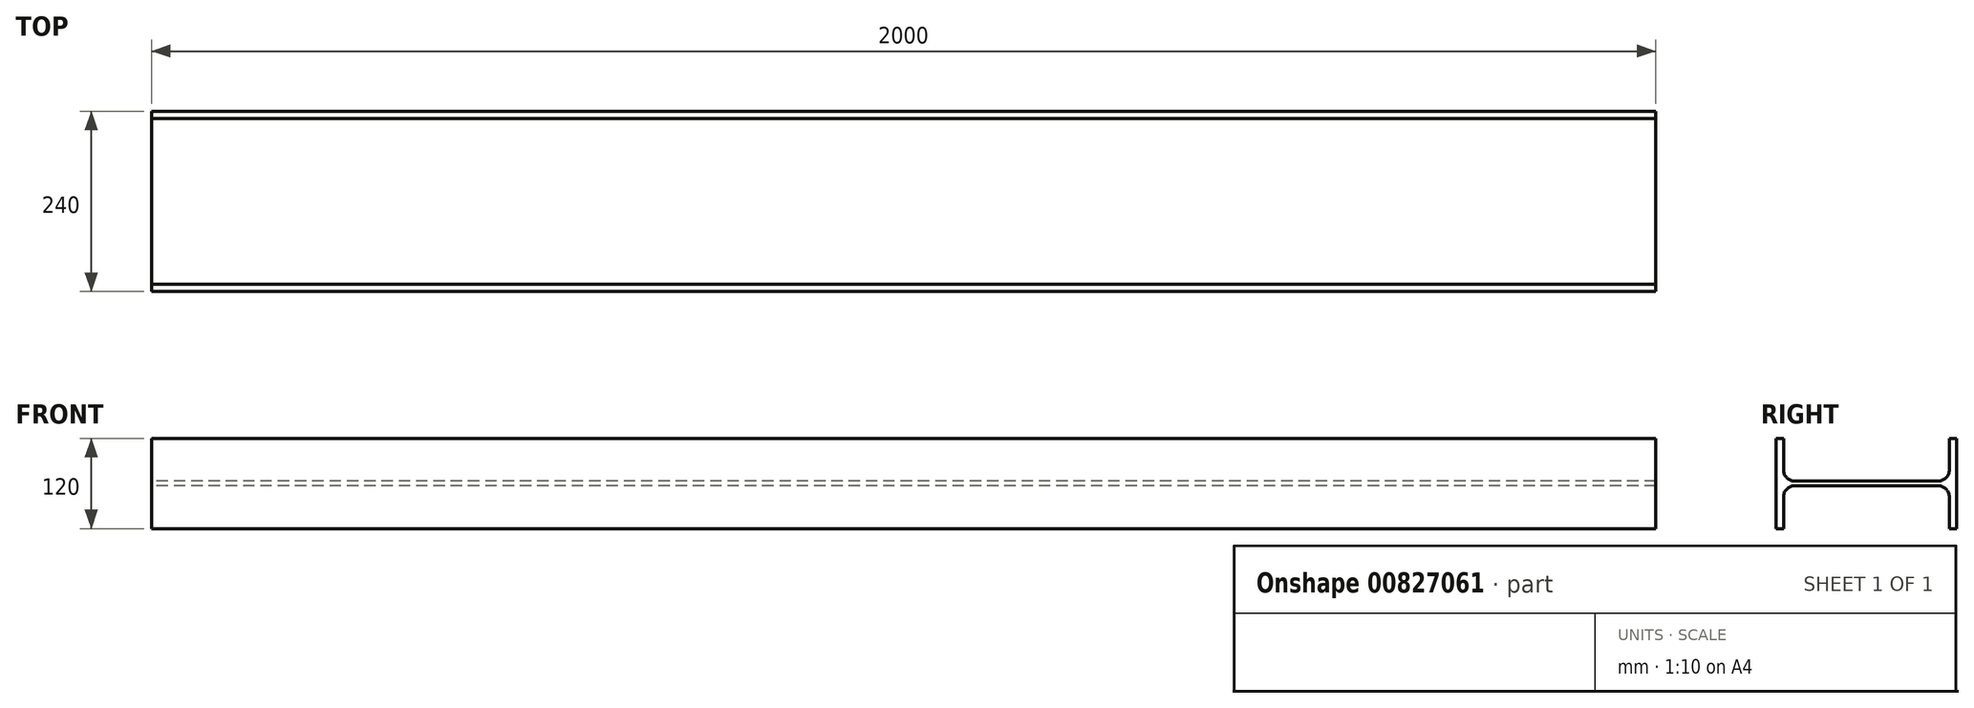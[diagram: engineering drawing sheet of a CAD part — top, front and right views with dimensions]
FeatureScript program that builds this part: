
annotation { "Feature Type Name" : "Feature", "Feature Type Description" : "" }
export const myFeature = defineFeature(function(context is Context, id is Id, definition is map)
    precondition{}
    {
        {
            var Q0;
            Q0=qCreatedBy(makeId("Right.planeOp"),FACE);
            var sketch = newSketch(context, id + "F0", { "sketchPlane" : qUnion([Q0])});
            skLineSegment(sketch, "E0", {"start": v(120, 0) * mm, "end": v(-120, 0) * mm, "construction": true});
            skLineSegment(sketch, "E1", {"start": v(120, 60) * mm, "end": v(120, -60) * mm});
            skLineSegment(sketch, "E2", {"start": v(-120, 60) * mm, "end": v(-120, -60) * mm});
            skLineSegment(sketch, "E3", {"start": v(-120, -60) * mm, "end": v(-110.2, -60) * mm});
            skLineSegment(sketch, "E4", {"start": v(-110.2, -60) * mm, "end": v(-110.2, -18.1) * mm});
            skLineSegment(sketch, "E5", {"start": v(-110.2, 60) * mm, "end": v(-120, 60) * mm});
            skLineSegment(sketch, "E6", {"start": v(120, 60) * mm, "end": v(110.2, 60) * mm});
            skLineSegment(sketch, "E7", {"start": v(110.2, 60) * mm, "end": v(110.2, 18.1) * mm});
            skLineSegment(sketch, "E8", {"start": v(110.2, -60) * mm, "end": v(120, -60) * mm});
            skLineSegment(sketch, "E9", {"start": v(95.2, 3.1) * mm, "end": v(-95.2, 3.1) * mm});
            skLineSegment(sketch, "E10", {"start": v(95.2, -3.1) * mm, "end": v(-95.2, -3.1) * mm});
            skPoint(sketch, "E11.newPointA", {"position": v(110.2, -60) * mm});
            skArc(sketch, "E11.filletArc", {"start": v(95.2, 3.1) * mm, "mid": v(105.8, 7.5) * mm, "end": v(110.2, 18.1) * mm});
            skLineSegment(sketch, "E12", {"start": v(110.2, -18.1) * mm, "end": v(110.2, -60) * mm});
            skPoint(sketch, "E13.visualSharp", {"position": v(110.2, -3.1) * mm});
            skArc(sketch, "E13.filletArc", {"start": v(110.2, -18.1) * mm, "mid": v(105.8, -7.5) * mm, "end": v(95.2, -3.1) * mm});
            skPoint(sketch, "E14.newPointA", {"position": v(-110.2, 60) * mm});
            skArc(sketch, "E14.filletArc", {"start": v(-95.2, -3.1) * mm, "mid": v(-105.8, -7.5) * mm, "end": v(-110.2, -18.1) * mm});
            skLineSegment(sketch, "E15", {"start": v(-110.2, 60) * mm, "end": v(-110.2, 18.1) * mm});
            skPoint(sketch, "E16.visualSharp", {"position": v(-110.2, 3.1) * mm});
            skArc(sketch, "E16.filletArc", {"start": v(-110.2, 18.1) * mm, "mid": v(-105.8, 7.5) * mm, "end": v(-95.2, 3.1) * mm});
            skSolve(sketch);
        }
        {
            var Q0;
            Q0=makeQuery(id+"F0.imprint","IMPRINT",FACE,{"disambiguationData":[TD([[makeQuery(id+"F0.imprint","IMPRINT",EDGE,{"derivedFrom":sQuery(id+"F0.wireOp",EDGE,"E1")}),-1.0]])]});
            extrude(context, id + "F1", {"entities" : qUnion([Q0]), "endBound" : BoundingType.SYMMETRIC, "depth" : 2000 * mm, "offsetDistance" : 25 * mm});
        }
    });
